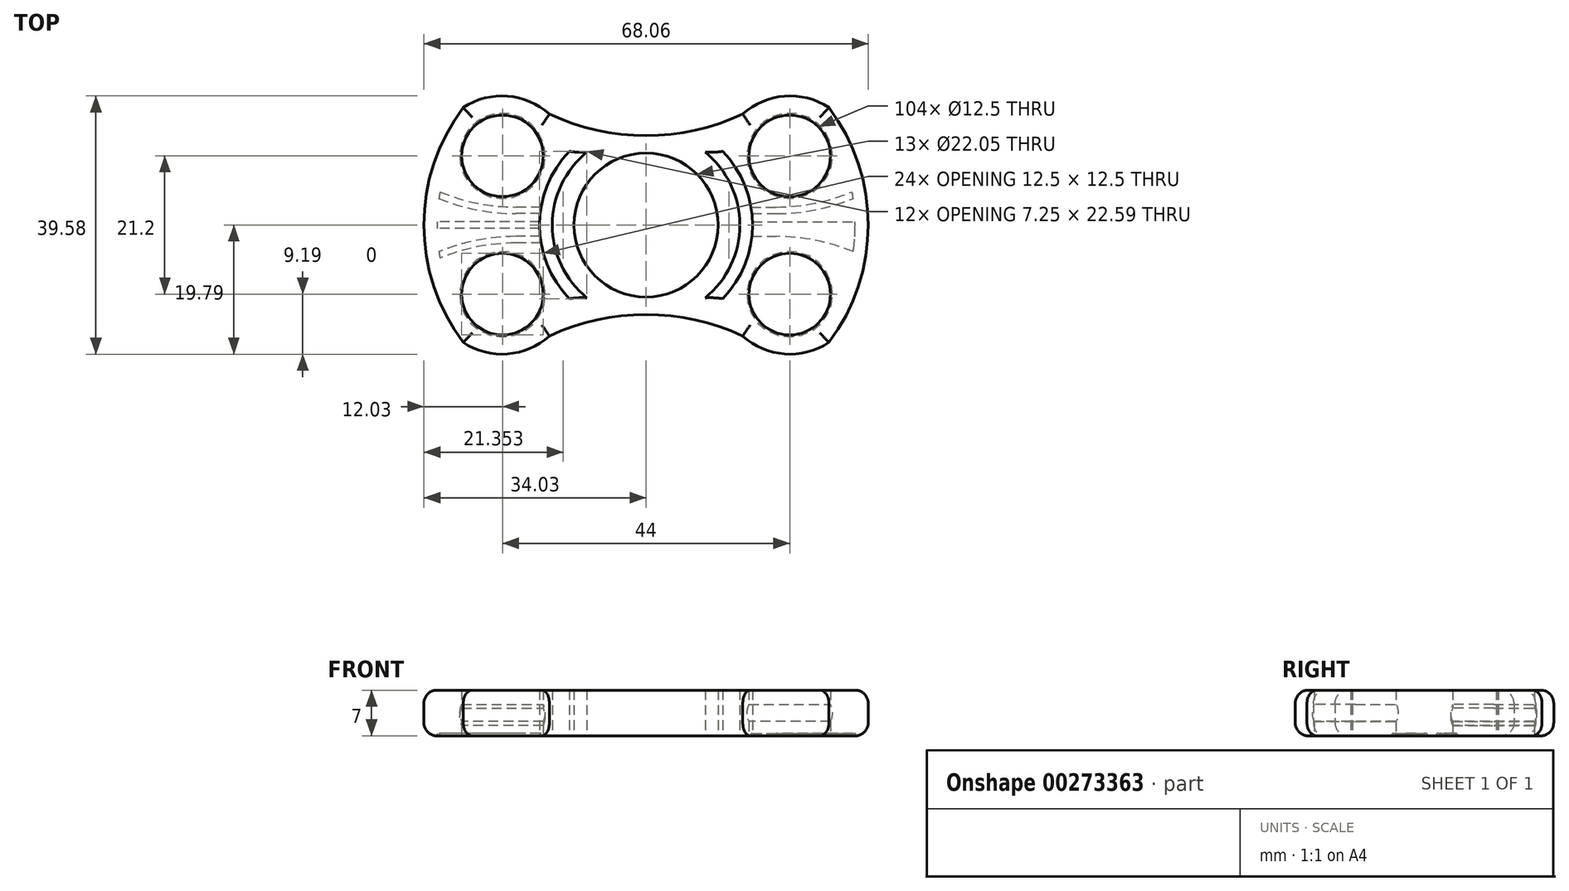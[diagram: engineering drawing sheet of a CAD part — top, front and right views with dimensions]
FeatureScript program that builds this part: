
annotation { "Feature Type Name" : "Feature", "Feature Type Description" : "" }
export const myFeature = defineFeature(function(context is Context, id is Id, definition is map)
    precondition{}
    {
        {
            var Q0;
            Q0=qCreatedBy(makeId("Top.planeOp"),FACE);
            var sketch = newSketch(context, id + "F0", { "sketchPlane" : qUnion([Q0])});
            skCircle(sketch, "E0", {"center": v(0, 0) * mm, "radius": 11.03 * mm});
            skCircle(sketch, "E1", {"center": v(-22, -10.6) * mm, "radius": 6.25 * mm});
            skCircle(sketch, "E2.MirrorC", {"center": v(-22, 10.6) * mm, "radius": 6.25 * mm});
            skLineSegment(sketch, "E3", {"start": v(-28, -18) * mm, "end": v(0, -18) * mm, "construction": true});
            skLineSegment(sketch, "E4.MirrorCS", {"start": v(-28, 18) * mm, "end": v(0, 18) * mm, "construction": true});
            skLineSegment(sketch, "E5", {"start": v(-32.94, -8) * mm, "end": v(0, -8) * mm, "construction": true});
            skLineSegment(sketch, "E6.MirrorCS", {"start": v(-32.94, 8) * mm, "end": v(0, 8) * mm, "construction": true});
            skCircle(sketch, "E7.MirrorC", {"center": v(22, 10.6) * mm, "radius": 6.25 * mm});
            skCircle(sketch, "E8.MirrorC", {"center": v(22, -10.6) * mm, "radius": 6.25 * mm});
            skArc(sketch, "E9", {"start": v(-28, 18) * mm, "mid": v(-34.03, 0) * mm, "end": v(-28, -18) * mm});
            skArc(sketch, "E10.MirrorCS", {"start": v(28, 18) * mm, "mid": v(34.03, 0) * mm, "end": v(28, -18) * mm});
            skLineSegment(sketch, "E11", {"start": v(-14.81, 17) * mm, "end": v(14.81, 17) * mm, "construction": true});
            skArc(sketch, "E12", {"start": v(-14.81, 17) * mm, "mid": v(0, 13.71) * mm, "end": v(14.81, 17) * mm});
            skArc(sketch, "E13.MirrorCS", {"start": v(-14.81, -17) * mm, "mid": v(0, -13.71) * mm, "end": v(14.81, -17) * mm});
            skArc(sketch, "E14.trimOffspring", {"start": v(-14.81, 17) * mm, "mid": v(-21.24, 19.76) * mm, "end": v(-28, 18) * mm});
            skPoint(sketch, "E15.orphan", {"position": v(-33.34, 6.38) * mm});
            skPoint(sketch, "E16.orphan", {"position": v(-33.34, -6.38) * mm});
            skArc(sketch, "E17.trimOffspring", {"start": v(-14.81, -17) * mm, "mid": v(-21.24, -19.76) * mm, "end": v(-28, -18) * mm});
            skArc(sketch, "E18.trimOffspring", {"start": v(14.81, -17) * mm, "mid": v(21.24, -19.76) * mm, "end": v(28, -18) * mm});
            skArc(sketch, "E19.trimOffspring", {"start": v(14.81, 17) * mm, "mid": v(21.24, 19.76) * mm, "end": v(28, 18) * mm});
            skPoint(sketch, "E20.orphan", {"position": v(33.34, -6.38) * mm});
            skPoint(sketch, "E21.orphan", {"position": v(33.34, 6.38) * mm});
            skArc(sketch, "E22", {"start": v(9.05, 11.17) * mm, "mid": v(10.4, 11.15) * mm, "end": v(11.76, 11.3) * mm});
            skArc(sketch, "E23.MirrorCS", {"start": v(9.05, -11.17) * mm, "mid": v(10.4, -11.15) * mm, "end": v(11.76, -11.3) * mm});
            skArc(sketch, "E24.trimOffspring", {"start": v(11.76, -11.3) * mm, "mid": v(16.3, 0) * mm, "end": v(11.76, 11.3) * mm});
            skArc(sketch, "E25.MirrorCS", {"start": v(-11.76, -11.3) * mm, "mid": v(-16.3, 0) * mm, "end": v(-11.76, 11.3) * mm});
            skArc(sketch, "E26.MirrorCS", {"start": v(-9.05, 11.17) * mm, "mid": v(-10.4, 11.15) * mm, "end": v(-11.76, 11.3) * mm});
            skArc(sketch, "E27.MirrorCS", {"start": v(-9.05, -11.17) * mm, "mid": v(-10.4, -11.15) * mm, "end": v(-11.76, -11.3) * mm});
            skArc(sketch, "E28.trimOffspring", {"start": v(9.05, -11.17) * mm, "mid": v(14.38, 0) * mm, "end": v(9.05, 11.17) * mm});
            skArc(sketch, "E29.trimOffspring", {"start": v(-9.05, 11.17) * mm, "mid": v(-14.38, 0) * mm, "end": v(-9.05, -11.17) * mm});
            skPoint(sketch, "E30.orphan", {"position": v(-8.37, -11.23) * mm});
            skPoint(sketch, "E31.orphan", {"position": v(-8.37, 11.23) * mm});
            skSolve(sketch);
        }
        {
            var Q0;
            Q0=makeQuery(id+"F0.imprint","IMPRINT",FACE,{"disambiguationData":[TD([[makeQuery(id+"F0.imprint","IMPRINT",EDGE,{"derivedFrom":sQuery(id+"F0.wireOp",EDGE,"E0")}),-1.0]])]});
            extrude(context, id + "F1", {"entities" : qUnion([Q0]), "depth" : 7 * mm, "offsetDistance" : 25 * mm});
        }
        {
            var Q0;
            Q0=makeQuery(id+"F1.opExtrude","CAP_EDGE",EDGE,{"disambiguationData":[OSD([sQuery(id+"F0.wireOp",EDGE,"E13.MirrorCS")])],"isStart":false});
            var Q1;
            Q1=makeQuery(id+"F1.opExtrude","CAP_EDGE",EDGE,{"disambiguationData":[OSD([sQuery(id+"F0.wireOp",EDGE,"E17.trimOffspring")])],"isStart":false});
            var Q2;
            Q2=makeQuery(id+"F1.opExtrude","CAP_EDGE",EDGE,{"disambiguationData":[OSD([sQuery(id+"F0.wireOp",EDGE,"E9")])],"isStart":false});
            var Q3;
            Q3=makeQuery(id+"F1.opExtrude","CAP_EDGE",EDGE,{"disambiguationData":[OSD([sQuery(id+"F0.wireOp",EDGE,"E14.trimOffspring")])],"isStart":false});
            var Q4;
            Q4=makeQuery(id+"F1.opExtrude","CAP_EDGE",EDGE,{"disambiguationData":[OSD([sQuery(id+"F0.wireOp",EDGE,"E12")])],"isStart":false});
            var Q5;
            Q5=makeQuery(id+"F1.opExtrude","CAP_EDGE",EDGE,{"disambiguationData":[OSD([sQuery(id+"F0.wireOp",EDGE,"E19.trimOffspring")])],"isStart":false});
            var Q6;
            Q6=makeQuery(id+"F1.opExtrude","CAP_EDGE",EDGE,{"disambiguationData":[OSD([sQuery(id+"F0.wireOp",EDGE,"E10.MirrorCS")])],"isStart":false});
            var Q7;
            Q7=makeQuery(id+"F1.opExtrude","CAP_EDGE",EDGE,{"disambiguationData":[OSD([sQuery(id+"F0.wireOp",EDGE,"E18.trimOffspring")])],"isStart":false});
            var Q8;
            Q8=makeQuery(id+"F1.opExtrude","CAP_EDGE",EDGE,{"disambiguationData":[OSD([sQuery(id+"F0.wireOp",EDGE,"E18.trimOffspring")])],"isStart":true});
            var Q9;
            Q9=makeQuery(id+"F1.opExtrude","CAP_EDGE",EDGE,{"disambiguationData":[OSD([sQuery(id+"F0.wireOp",EDGE,"E10.MirrorCS")])],"isStart":true});
            var Q10;
            Q10=makeQuery(id+"F1.opExtrude","CAP_EDGE",EDGE,{"disambiguationData":[OSD([sQuery(id+"F0.wireOp",EDGE,"E13.MirrorCS")])],"isStart":true});
            var Q11;
            Q11=makeQuery(id+"F1.opExtrude","CAP_EDGE",EDGE,{"disambiguationData":[OSD([sQuery(id+"F0.wireOp",EDGE,"E17.trimOffspring")])],"isStart":true});
            var Q12;
            Q12=makeQuery(id+"F1.opExtrude","CAP_EDGE",EDGE,{"disambiguationData":[OSD([sQuery(id+"F0.wireOp",EDGE,"E9")])],"isStart":true});
            var Q13;
            Q13=makeQuery(id+"F1.opExtrude","CAP_EDGE",EDGE,{"disambiguationData":[OSD([sQuery(id+"F0.wireOp",EDGE,"E14.trimOffspring")])],"isStart":true});
            var Q14;
            Q14=makeQuery(id+"F1.opExtrude","CAP_EDGE",EDGE,{"disambiguationData":[OSD([sQuery(id+"F0.wireOp",EDGE,"E19.trimOffspring")])],"isStart":true});
            var Q15;
            Q15=makeQuery(id+"F1.opExtrude","CAP_EDGE",EDGE,{"disambiguationData":[OSD([sQuery(id+"F0.wireOp",EDGE,"E12")])],"isStart":true});
            fillet(context, id + "F2", {"entities" : qUnion([Q0, Q1, Q2, Q3, Q4, Q5, Q6, Q7, Q8, Q9, Q10, Q11, Q12, Q13, Q14, Q15]), "radius" : 2 * mm, "tangentPropagation" : true, "allowEdgeOverflow" : false});
        }
        {
            var Q0;
            Q0=makeQuery(id+"F1.opExtrude","CAP_FACE",FACE,{"disambiguationData":[OSD([sQuery(id+"F0.wireOp",EDGE,"E0"),sQuery(id+"F0.wireOp",EDGE,"E1"),sQuery(id+"F0.wireOp",EDGE,"E2.MirrorC"),sQuery(id+"F0.wireOp",EDGE,"E7.MirrorC"),sQuery(id+"F0.wireOp",EDGE,"E8.MirrorC"),sQuery(id+"F0.wireOp",EDGE,"E9"),sQuery(id+"F0.wireOp",EDGE,"E10.MirrorCS"),sQuery(id+"F0.wireOp",EDGE,"E12"),sQuery(id+"F0.wireOp",EDGE,"E13.MirrorCS"),sQuery(id+"F0.wireOp",EDGE,"E14.trimOffspring"),sQuery(id+"F0.wireOp",EDGE,"E17.trimOffspring"),sQuery(id+"F0.wireOp",EDGE,"E18.trimOffspring"),sQuery(id+"F0.wireOp",EDGE,"E19.trimOffspring"),sQuery(id+"F0.wireOp",EDGE,"E22"),sQuery(id+"F0.wireOp",EDGE,"E23.MirrorCS"),sQuery(id+"F0.wireOp",EDGE,"f44a3dca-47a0-4530-a6ff-1fe1c9efb6ec.trimOffspring"),sQuery(id+"F0.wireOp",EDGE,"E24.trimOffspring"),sQuery(id+"F0.wireOp",EDGE,"ec64cd17-b78f-4b4f-86ed-a2804c1d69460.MirrorCS"),sQuery(id+"F0.wireOp",EDGE,"E25.MirrorCS"),sQuery(id+"F0.wireOp",EDGE,"E26.MirrorCS"),sQuery(id+"F0.wireOp",EDGE,"E27.MirrorCS")])],"isStart":true});
            var sketch = newSketch(context, id + "F3", { "sketchPlane" : qUnion([Q0])});
            skLineSegment(sketch, "E32", {"start": v(-16.07, 2.75) * mm, "end": v(-19.95, 2.75) * mm});
            skArc(sketch, "E33", {"start": v(-31.56, 5.09) * mm, "mid": v(-25.87, 3.34) * mm, "end": v(-19.95, 2.75) * mm});
            skLineSegment(sketch, "E34.0", {"start": v(-16.19, 1.75) * mm, "end": v(-19.95, 1.75) * mm});
            skArc(sketch, "E34.1", {"start": v(-31.73, 4.08) * mm, "mid": v(-25.95, 2.34) * mm, "end": v(-19.95, 1.75) * mm});
            skArc(sketch, "E35", {"start": v(-31.56, 5.09) * mm, "mid": v(-31.65, 4.58) * mm, "end": v(-31.73, 4.08) * mm});
            skArc(sketch, "E36", {"start": v(-16.19, 1.75) * mm, "mid": v(-16.12, 2.25) * mm, "end": v(-16.07, 2.75) * mm});
            skLineSegment(sketch, "E37.MirrorCS", {"start": v(-16.19, -1.75) * mm, "end": v(-19.95, -1.75) * mm});
            skLineSegment(sketch, "E38.MirrorCS", {"start": v(-16.07, -2.75) * mm, "end": v(-19.95, -2.75) * mm});
            skArc(sketch, "E39.MirrorCS", {"start": v(-31.56, -5.09) * mm, "mid": v(-25.87, -3.34) * mm, "end": v(-19.95, -2.75) * mm});
            skArc(sketch, "E40.MirrorCS", {"start": v(-31.73, -4.08) * mm, "mid": v(-25.95, -2.34) * mm, "end": v(-19.95, -1.75) * mm});
            skArc(sketch, "E41.MirrorCS", {"start": v(-31.56, -5.09) * mm, "mid": v(-31.65, -4.58) * mm, "end": v(-31.73, -4.08) * mm});
            skArc(sketch, "E42.MirrorCS", {"start": v(-16.19, -1.75) * mm, "mid": v(-16.12, -2.25) * mm, "end": v(-16.07, -2.75) * mm});
            skLineSegment(sketch, "E43", {"start": v(-16.3, 0.5) * mm, "end": v(-32.03, 0.5) * mm});
            skLineSegment(sketch, "E44.MirrorCS", {"start": v(-16.3, -0.5) * mm, "end": v(-32.03, -0.5) * mm});
            skArc(sketch, "E45.MirrorCS", {"start": v(31.56, -5.09) * mm, "mid": v(25.87, -3.34) * mm, "end": v(19.95, -2.75) * mm});
            skArc(sketch, "E46.MirrorCS", {"start": v(31.73, -4.08) * mm, "mid": v(25.95, -2.34) * mm, "end": v(19.95, -1.75) * mm});
            skLineSegment(sketch, "E47.MirrorCS", {"start": v(16.3, -0.5) * mm, "end": v(32.03, -0.5) * mm});
            skLineSegment(sketch, "E48.MirrorCS", {"start": v(16.3, 0.5) * mm, "end": v(32.03, 0.5) * mm});
            skArc(sketch, "E49.MirrorCS", {"start": v(31.73, 4.08) * mm, "mid": v(25.95, 2.34) * mm, "end": v(19.95, 1.75) * mm});
            skArc(sketch, "E50.MirrorCS", {"start": v(31.56, 5.09) * mm, "mid": v(25.87, 3.34) * mm, "end": v(19.95, 2.75) * mm});
            skLineSegment(sketch, "E51.MirrorCS", {"start": v(16.07, 2.75) * mm, "end": v(19.95, 2.75) * mm});
            skLineSegment(sketch, "E52.MirrorCS", {"start": v(16.19, 1.75) * mm, "end": v(19.95, 1.75) * mm});
            skArc(sketch, "E53.MirrorCS", {"start": v(16.19, 1.75) * mm, "mid": v(16.12, 2.25) * mm, "end": v(16.07, 2.75) * mm});
            skLineSegment(sketch, "E54.MirrorCS", {"start": v(16.19, -1.75) * mm, "end": v(19.95, -1.75) * mm});
            skLineSegment(sketch, "E55.MirrorCS", {"start": v(16.07, -2.75) * mm, "end": v(19.95, -2.75) * mm});
            skSolve(sketch);
        }
        {
            var Q0;
            {var subQ1=sQuery(id+"F3.wireOp",EDGE,"E38.MirrorCS");Q0=makeQuery(id+"F3.imprint","IMPRINT",FACE,{"disambiguationData":[TD([[makeQuery(id+"F3.imprint","IMPRINT",EDGE,{"derivedFrom":subQ1}),-1.0]])]});}
            var Q1;
            {var subQ0=sQuery(id+"F3.wireOp",EDGE,"E43");Q1=makeQuery(id+"F3.imprint","IMPRINT",FACE,{"disambiguationData":[TD([[makeQuery(id+"F3.imprint","IMPRINT",EDGE,{"derivedFrom":subQ0}),1.0]])]});}
            var Q2;
            {var subQ4=sQuery(id+"F3.wireOp",EDGE,"E32");Q2=makeQuery(id+"F3.imprint","IMPRINT",FACE,{"disambiguationData":[TD([[makeQuery(id+"F3.imprint","IMPRINT",EDGE,{"derivedFrom":subQ4}),1.0]])]});}
            var Q3;
            {var subQ1=sQuery(id+"F3.wireOp",EDGE,"E45.MirrorCS");Q3=makeQuery(id+"F3.imprint","IMPRINT",FACE,{"disambiguationData":[TD([[makeQuery(id+"F3.imprint","IMPRINT",EDGE,{"derivedFrom":subQ1}),-1.0]])]});}
            var Q4;
            {var subQ0=sQuery(id+"F3.wireOp",EDGE,"E47.MirrorCS");Q4=makeQuery(id+"F3.imprint","IMPRINT",FACE,{"disambiguationData":[TD([[makeQuery(id+"F3.imprint","IMPRINT",EDGE,{"derivedFrom":subQ0}),1.0]])]});}
            var Q5;
            {var subQ1=sQuery(id+"F3.wireOp",EDGE,"E49.MirrorCS");Q5=makeQuery(id+"F3.imprint","IMPRINT",FACE,{"disambiguationData":[TD([[makeQuery(id+"F3.imprint","IMPRINT",EDGE,{"derivedFrom":subQ1}),-1.0]])]});}
            extrude(context, id + "F4", {"entities" : qUnion([Q0, Q1, Q2, Q3, Q4, Q5]), "operationType" : NewBodyOperationType.REMOVE, "oppositeDirection" : true, "depth" : .4 * mm, "offsetDistance" : 25 * mm});
        }
        {
            var Q0;
            Q0=makeQuery(id+"F4.boolean.opBoolean","COPY",EDGE,{"derivedFrom":makeQuery(id+"F4.opExtrude","CAP_EDGE",EDGE,{"disambiguationData":[OSD([sQuery(id+"F3.wireOp",EDGE,"E34.1")])],"isStart":false})});
            var Q1;
            Q1=makeQuery(id+"F4.boolean.opBoolean","COPY",EDGE,{"derivedFrom":makeQuery(id+"F4.opExtrude","CAP_EDGE",EDGE,{"disambiguationData":[OSD([sQuery(id+"F3.wireOp",EDGE,"E43")])],"isStart":false})});
            var Q2;
            Q2=makeQuery(id+"F4.boolean.opBoolean","COPY",EDGE,{"derivedFrom":makeQuery(id+"F4.opExtrude","CAP_EDGE",EDGE,{"disambiguationData":[OSD([sQuery(id+"F3.wireOp",EDGE,"E40.MirrorCS")])],"isStart":false})});
            var Q3;
            Q3=makeQuery(id+"F4.boolean.opBoolean","COPY",EDGE,{"derivedFrom":makeQuery(id+"F4.opExtrude","CAP_EDGE",EDGE,{"disambiguationData":[OSD([sQuery(id+"F3.wireOp",EDGE,"E44.MirrorCS")])],"isStart":false})});
            var Q4;
            Q4=makeQuery(id+"F4.boolean.opBoolean","COPY",EDGE,{"derivedFrom":makeQuery(id+"F4.opExtrude","CAP_EDGE",EDGE,{"disambiguationData":[OSD([sQuery(id+"F3.wireOp",EDGE,"E39.MirrorCS")])],"isStart":false})});
            var Q5;
            Q5=makeQuery(id+"F4.boolean.opBoolean","COPY",EDGE,{"derivedFrom":makeQuery(id+"F4.opExtrude","CAP_EDGE",EDGE,{"disambiguationData":[OSD([sQuery(id+"F3.wireOp",EDGE,"E33")])],"isStart":false})});
            var Q6;
            Q6=makeQuery(id+"F4.boolean.opBoolean","COPY",EDGE,{"derivedFrom":makeQuery(id+"F4.opExtrude","CAP_EDGE",EDGE,{"disambiguationData":[OSD([sQuery(id+"F3.wireOp",EDGE,"E50.MirrorCS")])],"isStart":false})});
            var Q7;
            Q7=makeQuery(id+"F4.boolean.opBoolean","COPY",EDGE,{"derivedFrom":makeQuery(id+"F4.opExtrude","CAP_EDGE",EDGE,{"disambiguationData":[OSD([sQuery(id+"F3.wireOp",EDGE,"E48.MirrorCS")])],"isStart":false})});
            var Q8;
            Q8=makeQuery(id+"F4.boolean.opBoolean","COPY",EDGE,{"derivedFrom":makeQuery(id+"F4.opExtrude","CAP_EDGE",EDGE,{"disambiguationData":[OSD([sQuery(id+"F3.wireOp",EDGE,"E46.MirrorCS")])],"isStart":false})});
            var Q9;
            Q9=makeQuery(id+"F4.boolean.opBoolean","COPY",EDGE,{"derivedFrom":makeQuery(id+"F4.opExtrude","CAP_EDGE",EDGE,{"disambiguationData":[OSD([sQuery(id+"F3.wireOp",EDGE,"E45.MirrorCS")])],"isStart":false})});
            var Q10;
            Q10=makeQuery(id+"F4.boolean.opBoolean","COPY",EDGE,{"derivedFrom":makeQuery(id+"F4.opExtrude","CAP_EDGE",EDGE,{"disambiguationData":[OSD([sQuery(id+"F3.wireOp",EDGE,"E47.MirrorCS")])],"isStart":false})});
            var Q11;
            Q11=makeQuery(id+"F4.boolean.opBoolean","COPY",EDGE,{"derivedFrom":makeQuery(id+"F4.opExtrude","CAP_EDGE",EDGE,{"disambiguationData":[OSD([sQuery(id+"F3.wireOp",EDGE,"E49.MirrorCS")])],"isStart":false})});
            fillet(context, id + "F5", {"entities" : qUnion([Q0, Q1, Q2, Q3, Q4, Q5, Q6, Q7, Q8, Q9, Q10, Q11]), "radius" : .4 * mm, "tangentPropagation" : true, "allowEdgeOverflow" : false});
        }
        {
            var Q0;
            Q0=qCreatedBy(makeId("Right.planeOp"),FACE);
            cPlane(context, id + "F6", {"entities" : qUnion([Q0]), "cplaneType" : CPlaneType.OFFSET, "offset" : 22 * mm, "width" : 150 * mm, "height" : 150 * mm});
        }
        {
            var Q0;
            Q0=qCreatedBy(id+"F6.planeOp",FACE);
            var sketch = newSketch(context, id + "F7", { "sketchPlane" : qUnion([Q0])});
            skLineSegment(sketch, "E56", {"start": v(0, 0) * mm, "end": v(0, 3.5) * mm, "construction": true});
            skLineSegment(sketch, "E57", {"start": v(0, 3.5) * mm, "end": v(10.6, 3.5) * mm, "construction": true});
            skCircle(sketch, "E58", {"center": v(10.6, 3.5) * mm, "radius": 6.35 * mm, "construction": true});
            skLineSegment(sketch, "E59", {"start": v(10.6, 3.5) * mm, "end": v(10.6, 12.32) * mm});
            skCircle(sketch, "E60", {"center": v(7, 3.5) * mm, "radius": 2.96 * mm});
            skSolve(sketch);
        }
        {
            var Q0;
            Q0=makeQuery(id+"F7.imprint","IMPRINT",FACE,{"disambiguationData":[TD([[makeQuery(id+"F7.imprint","IMPRINT",EDGE,{"derivedFrom":sQuery(id+"F7.wireOp",EDGE,"E60")}),1.0]])]});
            var Q1;
            Q1=sQuery(id+"F7.wireOp",EDGE,"E59");
            revolve(context, id + "F8", {"operationType" : NewBodyOperationType.REMOVE, "entities" : qUnion([Q0]), "axis" : qUnion([Q1]), "revolveType" : RevolveType.FULL, "oppositeDirection" : true});
        }
        {
            var Q0;
            Q0=qCreatedBy(id+"F6.planeOp",FACE);
            var sketch = newSketch(context, id + "F9", { "sketchPlane" : qUnion([Q0])});
            skLineSegment(sketch, "E61", {"start": v(0, 0) * mm, "end": v(0, 3.5) * mm, "construction": true});
            skLineSegment(sketch, "E62", {"start": v(0, 3.5) * mm, "end": v(-10.6, 3.5) * mm, "construction": true});
            skCircle(sketch, "E63", {"center": v(-7, 3.5) * mm, "radius": 2.96 * mm});
            skLineSegment(sketch, "E64", {"start": v(-10.6, 3.5) * mm, "end": v(-10.6, 12.65) * mm});
            skSolve(sketch);
        }
        {
            var Q0;
            Q0=makeQuery(id+"F9.imprint","IMPRINT",FACE,{"disambiguationData":[TD([[makeQuery(id+"F9.imprint","IMPRINT",EDGE,{"derivedFrom":sQuery(id+"F9.wireOp",EDGE,"E63")}),1.0]])]});
            var Q1;
            Q1=sQuery(id+"F9.wireOp",EDGE,"E64");
            revolve(context, id + "F10", {"operationType" : NewBodyOperationType.REMOVE, "entities" : qUnion([Q0]), "axis" : qUnion([Q1]), "revolveType" : RevolveType.FULL, "oppositeDirection" : true});
        }
        {
            var Q0;
            Q0=qCreatedBy(makeId("Right.planeOp"),FACE);
            cPlane(context, id + "F11", {"entities" : qUnion([Q0]), "cplaneType" : CPlaneType.OFFSET, "offset" : 22 * mm, "oppositeDirection" : true, "width" : 150 * mm, "height" : 150 * mm});
        }
        {
            var Q0;
            Q0=qCreatedBy(id+"F11.planeOp",FACE);
            var sketch = newSketch(context, id + "F12", { "sketchPlane" : qUnion([Q0])});
            skLineSegment(sketch, "E65", {"start": v(0, 0) * mm, "end": v(0, 3.5) * mm, "construction": true});
            skLineSegment(sketch, "E66", {"start": v(0, 3.5) * mm, "end": v(-10.6, 3.5) * mm, "construction": true});
            skCircle(sketch, "E67", {"center": v(-7, 3.5) * mm, "radius": 2.96 * mm});
            skLineSegment(sketch, "E68", {"start": v(-10.6, 3.5) * mm, "end": v(-10.6, 8.85) * mm});
            skSolve(sketch);
        }
        {
            var Q0;
            Q0=makeQuery(id+"F12.imprint","IMPRINT",FACE,{"disambiguationData":[TD([[makeQuery(id+"F12.imprint","IMPRINT",EDGE,{"derivedFrom":sQuery(id+"F12.wireOp",EDGE,"E67")}),1.0]])]});
            var Q1;
            Q1=sQuery(id+"F12.wireOp",EDGE,"E68");
            revolve(context, id + "F13", {"operationType" : NewBodyOperationType.REMOVE, "entities" : qUnion([Q0]), "axis" : qUnion([Q1]), "revolveType" : RevolveType.FULL, "oppositeDirection" : true});
        }
        {
            var Q0;
            Q0=qCreatedBy(id+"F11.planeOp",FACE);
            var sketch = newSketch(context, id + "F14", { "sketchPlane" : qUnion([Q0])});
            skLineSegment(sketch, "E69", {"start": v(0, -0.6) * mm, "end": v(0, 2.9) * mm, "construction": true});
            skLineSegment(sketch, "E70", {"start": v(0, 2.9) * mm, "end": v(10.6, 2.9) * mm, "construction": true});
            skCircle(sketch, "E71", {"center": v(7, 2.9) * mm, "radius": 2.96 * mm});
            skLineSegment(sketch, "E72", {"start": v(10.6, 2.9) * mm, "end": v(10.6, 13.05) * mm});
            skSolve(sketch);
        }
        {
            var Q0;
            Q0=makeQuery(id+"F14.imprint","IMPRINT",FACE,{"disambiguationData":[TD([[makeQuery(id+"F14.imprint","IMPRINT",EDGE,{"derivedFrom":sQuery(id+"F14.wireOp",EDGE,"E71")}),1.0]])]});
            var Q1;
            Q1=sQuery(id+"F14.wireOp",EDGE,"E72");
            revolve(context, id + "F15", {"operationType" : NewBodyOperationType.REMOVE, "entities" : qUnion([Q0]), "axis" : qUnion([Q1]), "revolveType" : RevolveType.FULL, "oppositeDirection" : true});
        }
    });
